# Revit family: IS_Conca_T3809_BIM_NL
name_source: partatom
category: Plumbing Fixtures
units: mm (PartAtom-declared; Revit-internal decimal feet)

## family parameters
Always vertical = No
Cut with Voids When Loaded = No
OmniClass Number = 23.45.05.14.14
OmniClass Title = Sinks/Lavatories
Part Type = Normal
Room Calculation Point = No
Round Connector Dimension = Use Diameter
Shared = No
Work Plane-Based = No

## types (1)
- T380901 - CONCA WASHBASIN 1200 MM WITH 1 BOWL, WITHOUT OVERFLOW - WHITE GLOSSY.
    Accessories = https://www.idealstandard.nl
    Afmetingen = 1200 x 450 x 172 mm
    AfstandsEenheid = Millimeter
    Afwerking = Weiß
    AreaUnits = Millimetres
    Artikelnummer = T380901
    Artikelomschrijving = Conca Waschbecken 1200 mm mit 1 Becken, ohne Überlauf - Weiß glänzend.
    Artikelreferentie = CONCA WASHBASIN 1200 MM WITH 1 BOWL, WITHOUT OVERFLOW - WHITE GLOSSY.
    Auteur = Ideal Standard
    BIMObjectName = IS_IdealStandard_Wall-hungwashbasins_Conca_T3809
    BIMobject category = Wash Basins
    BIMobject category code = wash-basins
    BIMobject main category = Sanitary
    BIMobject main category code = sanitary
    BarCode = 8014140458258
    Beschrijvinggarantie = Herstellergarantie
    BimObjectNaam = IS_IdealStandard_Wall-hungwashbasins_Conca_T3809
    Brand = Ideal Standard
    Brand url = http://www.idealstandard.nl
    Breedte = 1200
    BrutoGewicht = 0
    Color = Weiß
    ConnectionType = Plumbing
    Cost = 0 $
    CurrencyUnit = €
    CurrentRevision = 1
    Date of publishing = 07/10/2021
    Description = Conca Washbasin 1200 mm with 1 bowl, without overflow - White glossy.
    Diepte = 450 mm
    DurationUnit = Years
    DuurEenheid = Jahre
    Edition number = 1
    Eigenschappen = Waschtisch 1200 mm, Vitreous China, 1 Becken, Befestigungsart: Steckbolzen, Mit Markenlogo, Weiß glänzend.
    ExpectedLife = 99
    Features = Washbasin 1200 mm, Vitreous China, 1 bowl, Type of fastening: Plug bolts, With brand logo, White glossy.
    Finish = Weiß
    GTIN code = https://8014140458258
    Garantieonderdelen = 5
    Garantieunits = Jahren
    GemaaktOp = 07/10/2021
    GrootteAfvoergat = 0
    Help = https://www.idealstandard.nl
    Hoogte = 172.004371970076
    Hulp = https://www.idealstandard.nl
    IFC Classification = Sanitary Terminal
    IfcExportAs = IfcSanitaryTerminalType
    IfcExportType = WASHHANDBASIN
    Installatieinstructies = https://www.idealstandard.nl
    Installation instructions = https://www.idealstandard.nl
    InstallationInstructions = https://www.idealstandard.nl
    IsBuiltIn = No
    Kleur = Weiß
    Lengte = 450 mm
    LinearUnits = Millimetres
    MainColor = white
    MaintenanceInformation = https://www.idealstandard.nl
    Manufacturer = Ideal Standard
    Manufacturer name = Ideal Standard
    ManufacturerURL = http://www.idealstandard.nl
    Masterformat 2014 Code = 33 47 26.16
    Masterformat 2014 Description = Retention Basin
    Materiaal = Fireclay
    Material = Fireclay
    Material main = Fireclay
    MaterialThickness = 0 mm  [stored 0 ft]
    Merk = Ideal Standard
    Model = T380901
    ModelNumber = T380901
    ModelReference = CONCA WASHBASIN 1200 MM WITH 1 BOWL, WITHOUT OVERFLOW - WHITE GLOSSY.
    Montageinstuctie = https://www.idealstandard.nl
    NBS Reference Code = 45-35-70/369
    NBS Reference Description = Wall hung wash basins
    Name = Wall-hungwashbasins_Conca_T3809_IdealStandard
    NettWeight = 32
    Nettogewicht = 0
    NominalDepth = 450 mm
    NominalHeight = 172 mm
    NominalWidth = 1200 mm
    OmniClass Code = 23-39 29 13 21 19
    OmniClass Description = Surface Water Retention Basins
    Ophangingwastafel = wandhängendes Waschbecken
    OppervlakteEenheid = Millimeter
    Product Guid = 3ba32ed1-4c99-418f-8982-941076a6e1ef
    Product SKU = T3809
    Product certification = https://www.idealstandard.nl
    Product data url = https://bimobject.com
    Product family = Conca
    Product group = Wash-Basin
    Product name = Conca New consolle basin 120 without tapholes.
    Product url = https://www.idealstandard.nl
    ProductInformation = https://www.idealstandard.nl
    Productinformatie = https://www.idealstandard.nl
    QR code = http://bimobject.com
    Referentie = T380901
    Revisie = 1
    Shape = sculpt
    Size = 1200 x 450 x 172 mm
    SpareParts = https://www.idealstandard.nl
    Technical description = https://www.idealstandard.nl
    Telefoonnummer = 077 355 08 08
    Typeconnectie = Installation
    Typewastafel = wandhängendes Waschbecken
    UNSPSC Code = 301815
    URL = http://www.idealstandard.nl
    Uniclass 1.4 Code = L7212
    Uniclass 1.4 Description = Washbasins
    Uniclass 2.0 Code = PR-31-79
    Uniclass 2.0 Description = Sinks, Wash Basins And Troughs
    Uniclass 2015 Code = Pr_40_20_96_96
    Uniclass 2015 Name = Wall-hung washbasins
    Uniclass2015Beschrijving = Wall-hung washbasins
    Uniclass2015Code = Pr_40_20_96_96
    Uniclass2015Referentie = Pr_40_20_96_96
    Uniclass2015Title = Wall-hung washbasins
    Uniclass2015Version = v1.22
    Uniformat II Code = D2010
    Uniformat II Description = Plumbing Fixtures
    Urlproducent = http://www.idealstandard.nl
    ValutaEenheid = Euro
    Versie = 1
    Version = 1
    Vervangingskosten = 0
    VolumeUnits = Litres
    Volumeunits = Liter
    Vorm = bildhauen
    WRASURL = https://www.wrasapprovals.co.uk
    WarrantyDescription = manufacturer warranty
    WarrantyDurationUnit = Years
    WashHandBasinMounting = Wall-Hung
    WashHandBasinType = Wall-Hung
    Wisselstukken = https://www.idealstandard.nl
    Youtube clip = https://www.youtube.com

note: [stored X ft] marks values corroborated as IEEE doubles in the binary element streams (Revit-internal decimal feet)

## geometry (parser evidence)
native form markers: Sweep x3
no freeform markers — native parametric forms only
